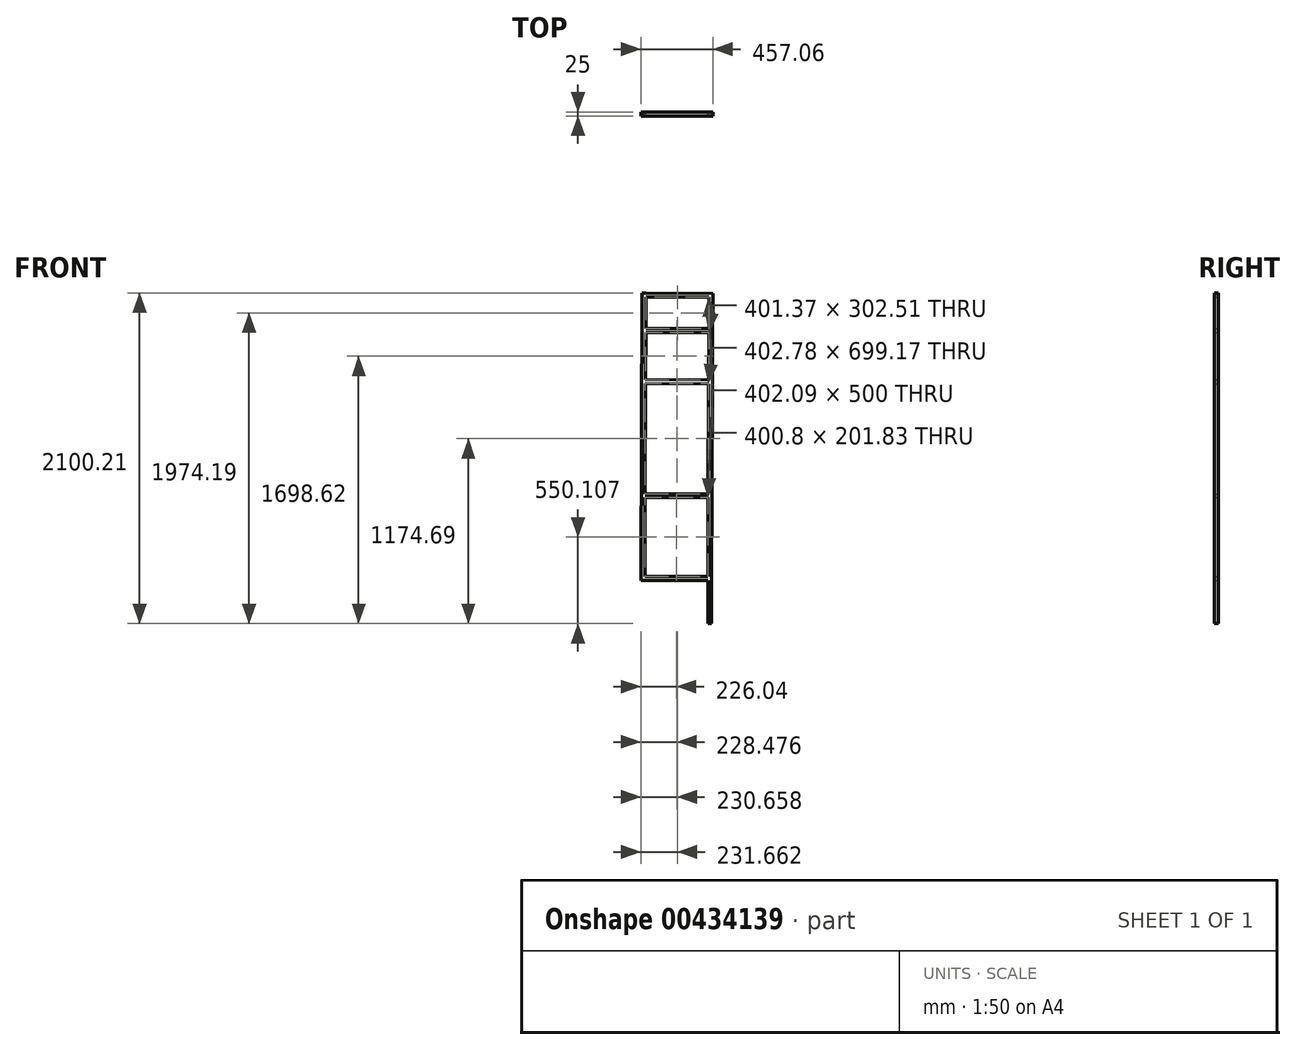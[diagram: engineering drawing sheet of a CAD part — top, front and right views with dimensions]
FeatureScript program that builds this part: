
annotation { "Feature Type Name" : "Feature", "Feature Type Description" : "" }
export const myFeature = defineFeature(function(context is Context, id is Id, definition is map)
    precondition{}
    {
        {
            var Q0;
            Q0=qCreatedBy(makeId("Front.planeOp"),FACE);
            var sketch = newSketch(context, id + "F0", { "sketchPlane" : qUnion([Q0])});
            skPoint(sketch, "E0.middle", {"position": v(0, 0) * mm});
            skLineSegment(sketch, "E1", {"start": v(-176.27, 875.7) * mm, "end": v(223.73, 873.88) * mm});
            skLineSegment(sketch, "E2", {"start": v(-177.56, 550.7) * mm, "end": v(222.44, 547.96) * mm});
            skLineSegment(sketch, "E3", {"start": v(-180.45, -174.3) * mm, "end": v(219.55, -174.3) * mm});
            skLineSegment(sketch, "E4.0", {"start": v(-207.53, -699.2) * mm, "end": v(-205.44, -174.2) * mm});
            skLineSegment(sketch, "E4.1", {"start": v(-202.56, 550.8) * mm, "end": v(-205.44, -174.2) * mm});
            skLineSegment(sketch, "E4.2", {"start": v(-202.56, 550.8) * mm, "end": v(-201.27, 875.8) * mm});
            skLineSegment(sketch, "E4.3", {"start": v(-200.37, 1100.8) * mm, "end": v(-201.27, 875.8) * mm});
            skLineSegment(sketch, "E5.0", {"start": v(-175.47, 1075.7) * mm, "end": v(224.53, 1074.11) * mm});
            skLineSegment(sketch, "E6", {"start": v(224.53, 1074.11) * mm, "end": v(223.73, 873.88) * mm});
            skLineSegment(sketch, "E7", {"start": v(223.82, 848.88) * mm, "end": v(222.44, 547.96) * mm});
            skLineSegment(sketch, "E8", {"start": v(222.34, 523.29) * mm, "end": v(219.55, -174.3) * mm});
            skLineSegment(sketch, "E9", {"start": v(222.34, 523.29) * mm, "end": v(-177.66, 524.88) * mm});
            skLineSegment(sketch, "E10", {"start": v(-200.37, 1100.8) * mm, "end": v(-175.37, 1100.7) * mm});
            skLineSegment(sketch, "E11", {"start": v(223.82, 848.88) * mm, "end": v(-176.37, 850.47) * mm});
            skLineSegment(sketch, "E12.0", {"start": v(249.53, 1074.02) * mm, "end": v(248.73, 873.78) * mm});
            skLineSegment(sketch, "E13.0", {"start": v(248.81, 848.76) * mm, "end": v(247.44, 547.85) * mm});
            skLineSegment(sketch, "E14.0", {"start": v(247.34, 523.19) * mm, "end": v(244.55, -174.4) * mm});
            skLineSegment(sketch, "E15.0", {"start": v(-180.45, -199.3) * mm, "end": v(219.55, -199.3) * mm});
            skLineSegment(sketch, "E16", {"start": v(219.55, -199.3) * mm, "end": v(217.47, -699.3) * mm});
            skLineSegment(sketch, "E17", {"start": v(-182.53, -699.3) * mm, "end": v(217.47, -699.3) * mm});
            skLineSegment(sketch, "E18.0", {"start": v(244.55, -199.4) * mm, "end": v(242.47, -699.4) * mm});
            skLineSegment(sketch, "E19.0", {"start": v(-182.53, -724.3) * mm, "end": v(217.47, -724.3) * mm});
            skLineSegment(sketch, "E20", {"start": v(242.47, -699.4) * mm, "end": v(242.47, -999.4) * mm});
            skLineSegment(sketch, "E21", {"start": v(242.47, -999.4) * mm, "end": v(217.47, -999.3) * mm});
            skLineSegment(sketch, "E22", {"start": v(217.47, -724.3) * mm, "end": v(217.47, -999.3) * mm});
            skLineSegment(sketch, "E23", {"start": v(249.53, 1074.02) * mm, "end": v(249.53, 1099.02) * mm});
            skLineSegment(sketch, "E24", {"start": v(-175.37, 1100.7) * mm, "end": v(249.53, 1099.02) * mm});
            skLineSegment(sketch, "E25", {"start": v(-207.53, -699.2) * mm, "end": v(-207.53, -724.2) * mm});
            skLineSegment(sketch, "E26", {"start": v(-182.53, -724.3) * mm, "end": v(-207.53, -724.2) * mm});
            skLineSegment(sketch, "E27", {"start": v(-175.47, 1075.7) * mm, "end": v(-176.27, 875.7) * mm});
            skLineSegment(sketch, "E28", {"start": v(-176.37, 850.47) * mm, "end": v(-177.56, 550.7) * mm});
            skLineSegment(sketch, "E29", {"start": v(-177.66, 524.88) * mm, "end": v(-180.45, -174.3) * mm});
            skLineSegment(sketch, "E30", {"start": v(-180.45, -199.3) * mm, "end": v(-182.53, -699.3) * mm});
            skLineSegment(sketch, "E31", {"start": v(244.55, -174.4) * mm, "end": v(244.55, -199.4) * mm});
            skLineSegment(sketch, "E32", {"start": v(247.34, 523.19) * mm, "end": v(247.44, 547.85) * mm});
            skLineSegment(sketch, "E33", {"start": v(248.81, 848.76) * mm, "end": v(248.73, 873.78) * mm});
            skSolve(sketch);
        }
        {
            var Q0;
            Q0 = qSketchRegion(id + "F0", true);
            extrude(context, id + "F1", {"entities" : qUnion([Q0]), "endBound" : BoundingType.SYMMETRIC, "depth" : 25 * mm});
        }
    });
